# Revit family: HDZXSA1-WALL
name_source: partatom
category: Lighting Fixtures
units: mm (PartAtom-declared; Revit-internal decimal feet)

## family parameters
Always vertical = Yes
Cut with Voids When Loaded = No
Host = Wall
Light Source = No
Maintain Annotation Orientation = No
Part Type = Normal
Room Calculation Point = No
Round Connector Dimension = Use Diameter
Shared = No

## types (1)
- HDZXSA1
    ACCESORY MATERIAL = LENS MATERIAL
    Default Elevation = 0' - 0"
    Description = HAZARDOUS EMERGENCY LIGHT
    FACE MATERIAL = FACE MATERIAL TRANSPARENT
    HOUSING MATERIAL = HOUSING MATERIAL
    LED BOARD MATERIAL = LED BOARD MATERIAL
    LED MATERIAL = LED MATERIAL
    LENS MATERIAL = LENS MATERIAL
    LETTER MATERIAL = LETTER MATERIAL RED
    Lamp = LED
    MOUNTING HEIGHT = 8' - 0"
    Manufacturer = BEGHELLI
    Model = HDZXSA1
    Type Image = HDZXSA1 IMAGE.png
    Wattage Comments = 5W

## geometry (parser evidence)
native form markers: Sweep x28
no freeform markers — native parametric forms only
